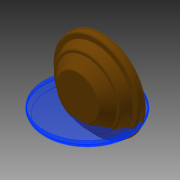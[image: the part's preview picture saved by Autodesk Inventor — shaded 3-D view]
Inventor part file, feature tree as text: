
AUTODESK INVENTOR PART (.ipt)
format: ipt  version: 2014 (Build 180170000, 170)  size: 183,808 bytes
history: native  units: in
note: dims shown in document units (in); Inventor stores cm internally (conversion verified against a paired STEP export)
features: other x3, sketch x2, extrude x1
ambient origin geometry x8: Origin, YZ Plane, XZ Plane, XY Plane, X Axis, Y Axis, Z Axis, Center Point
bodies: Solid1 (feature_tree)
feature tree (6):
  other  "DisceepXL_Case.ipt"
  extrude  "Extrusion1"  Depth=0.0801in
  other  "Solid1::DisceepXL_Case.ipt"
  other  "TaggingFeature1"
  sketch  "Sketch1"  dims[d0=0.3937in d1=0.0801in]
  sketch  "Sketch3"  dims[d2=0.0801in d3=0.0368in d4=0.0368in d5=1.0in d6=0.0in]
